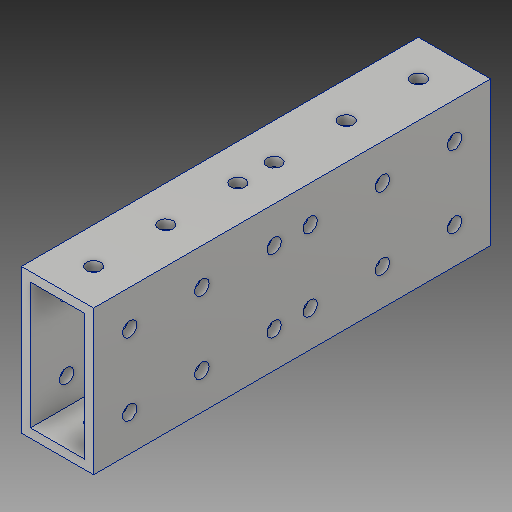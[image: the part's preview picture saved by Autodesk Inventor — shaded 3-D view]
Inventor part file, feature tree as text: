
AUTODESK INVENTOR PART (.ipt)
format: ipt  version: 2018 (Build 220112000, 112)  size: 182,784 bytes
history: native  units: in
note: dims shown in document units (in); Inventor stores cm internally (conversion verified against a paired STEP export)
features: extrude x3, sketch x3
ambient origin geometry x8: Origin, YZ Plane, XZ Plane, XY Plane, X Axis, Y Axis, Z Axis, Center Point
bodies: Solid1 (feature_tree)
feature tree (6):
  extrude  "Extrusion1"  Depth=2.0in
  extrude  "Extrusion2"  Depth=0.125in
  extrude  "Extrusion3"  Depth=0.125in
  sketch  "Sketch1"  dims[d0=1.0in d1=2.0in]
  sketch  "Sketch2"  dims[d2=0.125in d3=0.125in]
  sketch  "Sketch3"  dims[d4=0.125in d5=0.125in d6=5.5in d7=0.0in d8=0.5in d9=0.5in d10=0.5in d11=0.5in d12=1.0in d13=1.0in d14=1.0in d15=1.0in d16=0.2in d17=1.0in d18=0.0in d19=0.5in d20=1.0in d21=1.0in d22=0.5in d23=1.0in d24=1.0in d25=0.2in d26=4.375in d27=0.0in]
